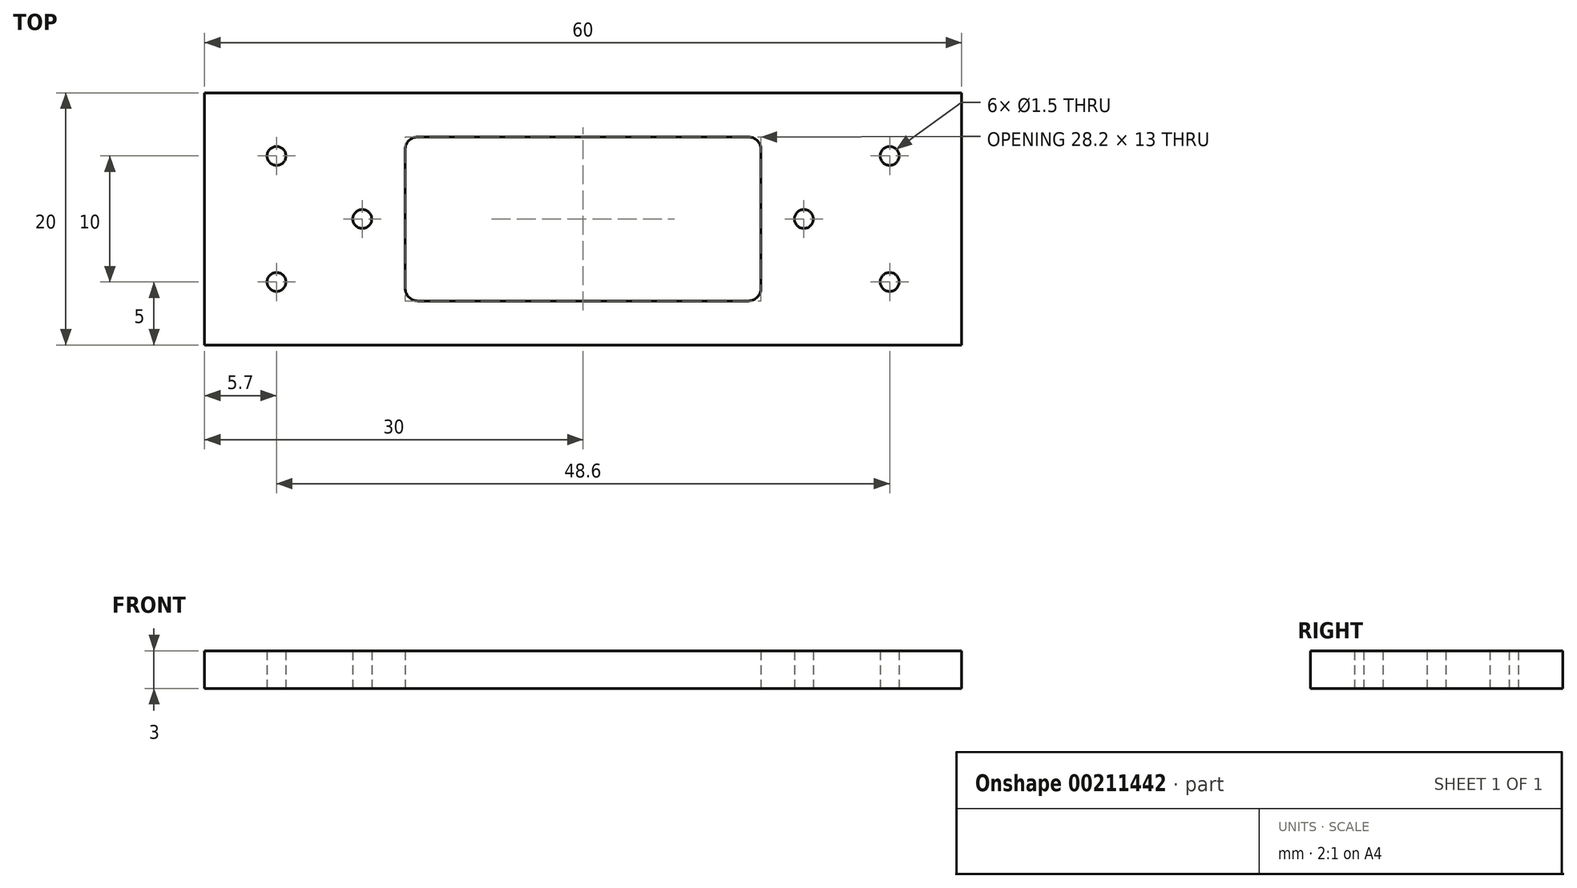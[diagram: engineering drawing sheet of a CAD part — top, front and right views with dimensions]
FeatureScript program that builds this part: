
annotation { "Feature Type Name" : "Feature", "Feature Type Description" : "" }
export const myFeature = defineFeature(function(context is Context, id is Id, definition is map)
    precondition{}
    {
        {
            var Q0;
            Q0=qCreatedBy(makeId("Top.planeOp"),FACE);
            var sketch = newSketch(context, id + "F0", { "sketchPlane" : qUnion([Q0])});
            skLineSegment(sketch, "E0.bottom", {"start": v(-30, 10) * mm, "end": v(30, 10) * mm});
            skLineSegment(sketch, "E0.top", {"start": v(-30, -10) * mm, "end": v(30, -10) * mm});
            skLineSegment(sketch, "E0.left", {"start": v(-30, 10) * mm, "end": v(-30, -10) * mm});
            skLineSegment(sketch, "E0.right", {"start": v(30, 10) * mm, "end": v(30, -10) * mm});
            skPoint(sketch, "E1.startSnap0", {"position": v(-30, 0) * mm});
            skLineSegment(sketch, "E2.bottom", {"start": v(-13.1, 6.5) * mm, "end": v(13.1, 6.5) * mm});
            skLineSegment(sketch, "E2.top", {"start": v(-13.1, -6.5) * mm, "end": v(13.1, -6.5) * mm});
            skLineSegment(sketch, "E2.left", {"start": v(-14.1, 5.5) * mm, "end": v(-14.1, -5.5) * mm});
            skLineSegment(sketch, "E2.right", {"start": v(14.1, 5.5) * mm, "end": v(14.1, -5.5) * mm});
            skLineSegment(sketch, "E3.left", {"start": v(-24.3, 5) * mm, "end": v(-24.3, -5) * mm});
            skCircle(sketch, "E4", {"center": v(-24.3, 5) * mm, "radius": 0.75 * mm});
            skCircle(sketch, "E5", {"center": v(-24.3, -5) * mm, "radius": 0.75 * mm});
            skCircle(sketch, "E6", {"center": v(24.3, 5) * mm, "radius": 0.75 * mm});
            skCircle(sketch, "E7", {"center": v(24.3, -5) * mm, "radius": 0.75 * mm});
            skPoint(sketch, "E8.endSnap0", {"position": v(14.1, 0) * mm});
            skCircle(sketch, "E9", {"center": v(17.5, 0) * mm, "radius": 0.75 * mm});
            skCircle(sketch, "E10.MirrorC", {"center": v(-17.5, 0) * mm, "radius": 0.75 * mm});
            skPoint(sketch, "E11.visualSharp", {"position": v(-14.1, 6.5) * mm});
            skArc(sketch, "E12.filletArc", {"start": v(-13.1, 6.5) * mm, "mid": v(-13.8, 6.2) * mm, "end": v(-14.1, 5.5) * mm});
            skPoint(sketch, "E13.visualSharp", {"position": v(14.1, 6.5) * mm});
            skArc(sketch, "E13.filletArc", {"start": v(14.1, 5.5) * mm, "mid": v(13.8, 6.2) * mm, "end": v(13.1, 6.5) * mm});
            skPoint(sketch, "E14.visualSharp", {"position": v(-14.1, -6.5) * mm});
            skArc(sketch, "E14.filletArc", {"start": v(-14.1, -5.5) * mm, "mid": v(-13.8, -6.2) * mm, "end": v(-13.1, -6.5) * mm});
            skPoint(sketch, "E15.visualSharp", {"position": v(14.1, -6.5) * mm});
            skArc(sketch, "E15.filletArc", {"start": v(13.1, -6.5) * mm, "mid": v(13.8, -6.2) * mm, "end": v(14.1, -5.5) * mm});
            skSolve(sketch);
        }
        {
            var Q0;
            Q0=makeQuery(id+"F0.imprint","IMPRINT",FACE,{"disambiguationData":[TD([[makeQuery(id+"F0.imprint","IMPRINT",EDGE,{"derivedFrom":sQuery(id+"F0.wireOp",EDGE,"E0.bottom")}),-1.0]])]});
            extrude(context, id + "F1", {"entities" : qUnion([Q0]), "depth" : 3 * mm});
        }
    });
